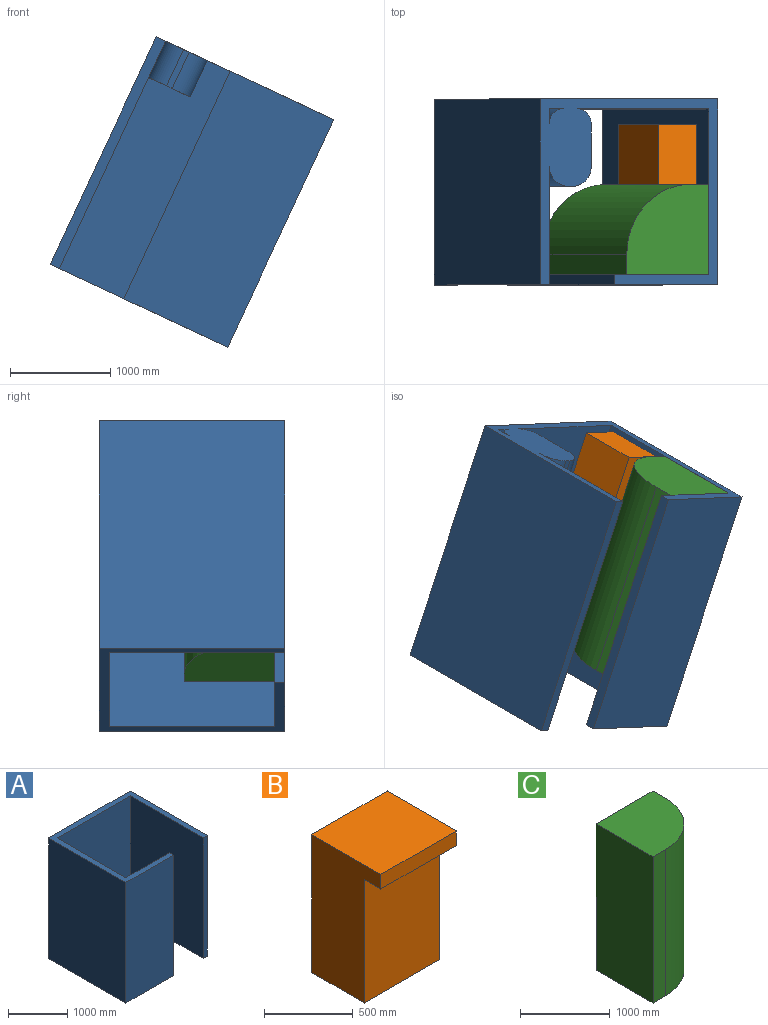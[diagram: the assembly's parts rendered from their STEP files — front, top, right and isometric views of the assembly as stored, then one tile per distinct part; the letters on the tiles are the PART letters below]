
ASSEMBLY  parts=3 mates=6
PART A: 19 faces, bbox 1950x1850x2500 mm
  f0: plane 2500x1140mm, normal (0,-1,0), area 2850000mm2, adj f1,f9,f10,f11
  f1: plane 2500x100mm, normal (1,0,0), area 250000mm2, adj f0,f2,f10,f11
  f2: plane 2500x1040mm, normal (0,1,0), area 2600000mm2, adj f1,f3,f10,f11
  f3: plane 2500x1650mm, normal (1,0,0), area 4125000mm2, adj f2,f4,f10,f11
  f4: plane 2500x1750mm, normal (0,-1,0), area 4311000mm2, adj f3,f5,f10,f11,f16,f17,f18
  f5: plane 2500x1750mm, normal (-1,0,0), area 4207000mm2, adj f4,f6,f10,f11,f12,f17,f18
  f6: plane 2500x100mm, normal (0,-1,0), area 250000mm2, adj f5,f7,f10,f11
  f7: plane 2500x1850mm, normal (1,0,0), area 4625000mm2, adj f6,f8,f10,f11
  f8: plane 2500x1950mm, normal (0,1,0), area 4875000mm2, adj f7,f9,f10,f11
  f9: plane 2500x1850mm, normal (-1,0,0), area 4625000mm2, adj f0,f8,f10,f11
  f10: plane 1950x1850mm, normal (0,0,1), area 649000mm2, adj f0,f1,f2,f3,f4,f5,f6,f7
  f11: plane 1950x1850mm, normal (0,0,-1), area 976374.8mm2, adj f0,f1,f2,f3,f4,f5,f6,f7
  f12: cylinder r=200mm len=400mm, axis (0,0,-1), area 125663.7mm2, adj f5,f11,f13,f18
  f13: plane 400x60mm, normal (0,-1,0), area 24000mm2, adj f11,f12,f14,f18
  f14: cylinder r=200mm len=400mm, axis (0,0,-1), area 125663.7mm2, adj f11,f13,f15,f18
  f15: plane 420x400mm, normal (-1,0,0), area 168000mm2, adj f11,f14,f16,f18
  f16: cylinder r=150mm len=400mm, axis (0,0,-1), area 94247.8mm2, adj f4,f11,f15,f18
  f17: cylinder r=150mm len=400mm, axis (0,0,-1), area 94247.8mm2, adj f4,f5,f11,f18
  f18: plane 770x460mm, normal (0,0,1), area 327374.8mm2, adj f4,f5,f12,f13,f14,f15,f16,f17
PART B: 8 faces, bbox 600x550x950 mm
  f0: plane 950x550mm, normal (1,0,0), area 412000mm2, adj f1,f3,f4,f5,f6,f7
  f1: plane 600x100mm, normal (0,-1,0), area 60000mm2, adj f0,f2,f4,f5
  f2: plane 950x550mm, normal (-1,0,0), area 412000mm2, adj f1,f3,f4,f5,f6,f7
  f3: plane 950x600mm, normal (0,1,0), area 570000mm2, adj f0,f2,f4,f7
  f4: plane 600x550mm, normal (0,0,1), area 330000mm2, adj f0,f1,f2,f3
  f5: plane 600x130mm, normal (0,0,-1), area 78000mm2, adj f0,f1,f2,f6
  f6: plane 850x600mm, normal (0,-1,0), area 510000mm2, adj f0,f2,f5,f7
  f7: plane 600x420mm, normal (0,0,-1), area 252000mm2, adj f0,f2,f3,f6
PART C: 7 faces, bbox 900x900x2000 mm
  f0: plane 2000x900mm, normal (-1,0,0), area 1800000mm2, adj f1,f4,f5,f6
  f1: plane 2000x900mm, normal (0,1,0), area 1800000mm2, adj f0,f2,f5,f6
  f2: plane 2000x200mm, normal (1,0,0), area 400000mm2, adj f1,f3,f5,f6
  f3: cylinder r=700mm len=2000mm, axis (0,0,-1), area 2199114.9mm2, adj f2,f4,f5,f6
  f4: plane 2000x200mm, normal (0,-1,0), area 400000mm2, adj f0,f3,f5,f6
  f5: plane 900x900mm, normal (0,0,1), area 704845.1mm2, adj f0,f1,f2,f3,f4
  f6: plane 900x900mm, normal (0,0,-1), area 704845.1mm2, adj f0,f1,f2,f3,f4
PLACE A rot(axis=(0,-1,0),155deg) t=(1215.7,1771.68,1668.39)mm fixed
PLACE B rot(axis=(0.7,-0.7,-0.15),162.4deg) t=(1261.02,2011.68,1647.26)mm
PLACE C rot(axis=(-0.7,-0.7,0.15),162.4deg) t=(1306.33,1821.68,1626.13)mm
MATE parallel B.f0 <-> C.f2  axis (0,-1,0) through (1502.03,1846.68,995.97)mm
MATE parallel A.f3 <-> C.f1  axis (-0.91,0,0.42) through (1480.45,1771.68,165.71)mm
MATE parallel C.f0 <-> A.f2  axis (0,-1,0) through (1178.26,946.68,582.47)mm
MATE parallel B.f1 <-> A.f3  axis (0.91,0,-0.42) through (1628.36,2146.68,482.92)mm
MATE parallel C.f6 <-> A.f11  axis (0.42,0,0.91) through (1640.58,1352.87,1470.26)mm
MATE parallel C.f6 <-> B.f7  axis (0.42,0,0.91) through (1640.58,1352.87,1470.26)mm
